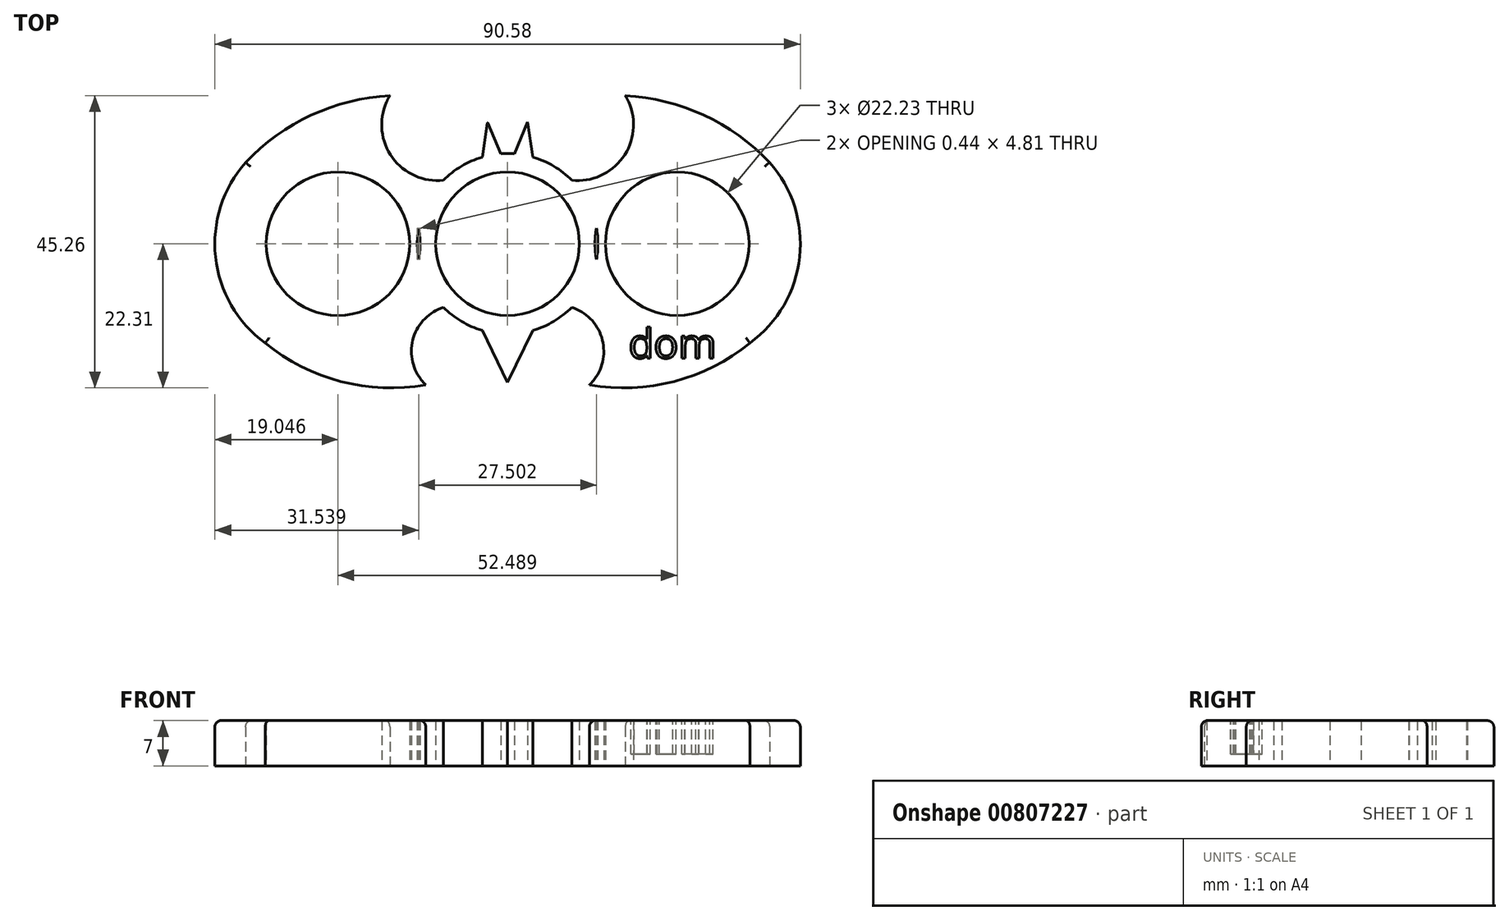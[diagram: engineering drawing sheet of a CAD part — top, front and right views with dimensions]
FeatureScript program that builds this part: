
annotation { "Feature Type Name" : "Feature", "Feature Type Description" : "" }
export const myFeature = defineFeature(function(context is Context, id is Id, definition is map)
    precondition{}
    {
        {
            var Q0;
            Q0=qCreatedBy(makeId("Top.planeOp"),FACE);
            var sketch = newSketch(context, id + "F0", { "sketchPlane" : qUnion([Q0])});
            skArc(sketch, "E0", {"start": v(-4.01, -13.38) * mm, "mid": v(7.2, 11.98) * mm, "end": v(-9.93, -9.83) * mm});
            skLineSegment(sketch, "E1", {"start": v(0, 0) * mm, "end": v(-26.24, 0) * mm});
            skLineSegment(sketch, "E2", {"start": v(0, 0) * mm, "end": v(26.24, 0) * mm});
            skArc(sketch, "E3", {"start": v(37.5, -15.37) * mm, "mid": v(45.18, -2.05) * mm, "end": v(40.53, 12.6) * mm});
            skArc(sketch, "E4", {"start": v(-18.2, 22.95) * mm, "mid": v(-30.36, 19.9) * mm, "end": v(-40.53, 12.6) * mm});
            skArc(sketch, "E5", {"start": v(-18.2, 22.95) * mm, "mid": v(-18.15, 13.81) * mm, "end": v(-9.93, 9.83) * mm});
            skArc(sketch, "E6.trimOffspring", {"start": v(-40.53, 12.6) * mm, "mid": v(-45.18, -2.05) * mm, "end": v(-37.5, -15.37) * mm});
            skArc(sketch, "E7.MirrorCS", {"start": v(18.2, 22.95) * mm, "mid": v(18.15, 13.81) * mm, "end": v(9.93, 9.83) * mm});
            skArc(sketch, "E8.MirrorCS", {"start": v(18.2, 22.95) * mm, "mid": v(30.36, 19.9) * mm, "end": v(40.53, 12.6) * mm});
            skArc(sketch, "E9", {"start": v(-37.5, -15.37) * mm, "mid": v(-25.79, -21.32) * mm, "end": v(-12.65, -21.85) * mm});
            skArc(sketch, "E10", {"start": v(-9.93, -9.83) * mm, "mid": v(-14.7, -15.06) * mm, "end": v(-12.65, -21.85) * mm});
            skArc(sketch, "E11.MirrorCS", {"start": v(9.93, -9.83) * mm, "mid": v(14.7, -15.06) * mm, "end": v(12.65, -21.85) * mm});
            skArc(sketch, "E12.MirrorCS", {"start": v(37.5, -15.37) * mm, "mid": v(25.79, -21.32) * mm, "end": v(12.65, -21.85) * mm});
            skPoint(sketch, "E13.end.orphan", {"position": v(2.34, 18.82) * mm});
            skPoint(sketch, "E14.orphan", {"position": v(3.92, 13.4) * mm});
            skPoint(sketch, "E15.end.orphan", {"position": v(-1.04, 13.93) * mm});
            skPoint(sketch, "E16.end.orphan", {"position": v(-2.23, 18.82) * mm});
            skPoint(sketch, "E17.MirrorCS.end.orphan", {"position": v(1.04, 13.93) * mm});
            skPoint(sketch, "E17.MirrorCS.start.orphan", {"position": v(2.23, 18.82) * mm});
            skPoint(sketch, "E18.end.orphan", {"position": v(-4.8, 18.35) * mm});
            skPoint(sketch, "E19.MirrorCS.end.orphan", {"position": v(4.8, 18.35) * mm});
            skLineSegment(sketch, "E20", {"start": v(-1.04, 13.93) * mm, "end": v(-3.1, 18.83) * mm});
            skLineSegment(sketch, "E21", {"start": v(-3.1, 18.83) * mm, "end": v(-3.92, 13.4) * mm});
            skLineSegment(sketch, "E22.MirrorCS", {"start": v(1.04, 13.93) * mm, "end": v(3.1, 18.83) * mm});
            skLineSegment(sketch, "E23.MirrorCS", {"start": v(3.1, 18.83) * mm, "end": v(3.92, 13.4) * mm});
            skPoint(sketch, "E24.end.orphan", {"position": v(0, -21.45) * mm});
            skPoint(sketch, "E24.start.orphan", {"position": v(-4.01, -13.38) * mm});
            skPoint(sketch, "E25.MirrorCS.start.orphan", {"position": v(4.01, -13.38) * mm});
            skPoint(sketch, "E26.MirrorCS.end.orphan", {"position": v(-3.92, -13.4) * mm});
            skPoint(sketch, "E26.MirrorCS.start.orphan", {"position": v(-3.1, -18.83) * mm});
            skLineSegment(sketch, "E27", {"start": v(-3.92, -13.4) * mm, "end": v(0, -21.45) * mm});
            skLineSegment(sketch, "E28.MirrorCS", {"start": v(3.92, -13.4) * mm, "end": v(0, -21.45) * mm});
            skLineSegment(sketch, "E29", {"start": v(0, 0) * mm, "end": v(45.3, 0) * mm});
            skArc(sketch, "E30", {"start": v(-13.76, -2.4) * mm, "mid": v(-13.53, 0) * mm, "end": v(-13.76, 2.4) * mm});
            skArc(sketch, "E31", {"start": v(13.76, 2.4) * mm, "mid": v(13.53, 0) * mm, "end": v(13.76, -2.4) * mm});
            skCircle(sketch, "E32", {"center": v(-26.24, 0) * mm, "radius": 11.11 * mm});
            skCircle(sketch, "E33", {"center": v(26.24, 0) * mm, "radius": 11.11 * mm});
            skCircle(sketch, "E34", {"center": v(0, 0) * mm, "radius": 13.97 * mm});
            skCircle(sketch, "E35", {"center": v(0, 0) * mm, "radius": 11.11 * mm});
            skSolve(sketch);
        }
        {
            var Q0;
            Q0=qSketchRegion(id+"F0",true);
            extrude(context, id + "F1", {"entities" : qUnion([Q0]), "depth" : 4.3 * mm, "offsetDistance" : 25.4 * mm});
        }
        {
            var Q0;
            Q0=qSketchRegion(id+"F0",true);
            extrude(context, id + "F2", {"entities" : qUnion([Q0]), "operationType" : NewBodyOperationType.ADD, "depth" : 7 * mm, "offsetDistance" : 25.4 * mm});
        }
        {
            var Q0;
            Q0=makeQuery(id+"F2.opExtrude","CAP_EDGE",EDGE,{"disambiguationData":[OSD([sQuery(id+"F0.wireOp",EDGE,"E6.trimOffspring")])],"isStart":false});
            var Q1;
            Q1=makeQuery(id+"F2.opExtrude","CAP_EDGE",EDGE,{"disambiguationData":[OSD([sQuery(id+"F0.wireOp",EDGE,"E4")])],"isStart":true});
            var Q2;
            Q2=makeQuery(id+"F2.opExtrude","CAP_EDGE",EDGE,{"disambiguationData":[OSD([sQuery(id+"F0.wireOp",EDGE,"E6.trimOffspring")])],"isStart":true});
            var Q3;
            Q3=makeQuery(id+"F2.opExtrude","CAP_EDGE",EDGE,{"disambiguationData":[OSD([sQuery(id+"F0.wireOp",EDGE,"E9")])],"isStart":true});
            fillet(context, id + "F3", {"entities" : qUnion([Q0, Q1, Q2, Q3]), "radius" : 1 * mm, "tangentPropagation" : true, "allowEdgeOverflow" : false});
        }
        {
            var Q0;
            Q0=makeQuery(id+"F2.opExtrude","CAP_EDGE",EDGE,{"disambiguationData":[OSD([sQuery(id+"F0.wireOp",EDGE,"E3")])],"isStart":false});
            var Q1;
            Q1=makeQuery(id+"F2.opExtrude","CAP_EDGE",EDGE,{"disambiguationData":[OSD([sQuery(id+"F0.wireOp",EDGE,"E3")])],"isStart":true});
            fillet(context, id + "F4", {"entities" : qUnion([Q0, Q1]), "radius" : 1 * mm, "tangentPropagation" : true, "allowEdgeOverflow" : false});
        }
        {
            var Q0;
            {var subQ0=sQuery(id+"F0.wireOp",EDGE,"E21");var subQ1=sQuery(id+"F0.wireOp",EDGE,"E20");Q0=makeQuery(id+"F2.boolean.opBoolean","MERGE",EDGE,{"derivedFrom":[makeQuery(id+"F1.opExtrude","SWEPT_EDGE",EDGE,{"disambiguationData":[OSD([subQ1,subQ0])]}),makeQuery(id+"F2.opExtrude","SWEPT_EDGE",EDGE,{"disambiguationData":[OSD([subQ1,subQ0])]})]});}
            fillet(context, id + "F5", {"entities" : qUnion([Q0]), "radius" : 0.04 * mm, "tangentPropagation" : true, "allowEdgeOverflow" : false});
        }
        {
            var Q0;
            Q0=makeQuery(id+"F2.opExtrude","CAP_FACE",FACE,{"disambiguationData":[OSD([sQuery(id+"F0.wireOp",EDGE,"E3"),sQuery(id+"F0.wireOp",EDGE,"E4"),sQuery(id+"F0.wireOp",EDGE,"E5"),sQuery(id+"F0.wireOp",EDGE,"E6.trimOffspring"),sQuery(id+"F0.wireOp",EDGE,"E7.MirrorCS"),sQuery(id+"F0.wireOp",EDGE,"E8.MirrorCS"),sQuery(id+"F0.wireOp",EDGE,"E9"),sQuery(id+"F0.wireOp",EDGE,"E10"),sQuery(id+"F0.wireOp",EDGE,"E11.MirrorCS"),sQuery(id+"F0.wireOp",EDGE,"E12.MirrorCS"),sQuery(id+"F0.wireOp",EDGE,"E20"),sQuery(id+"F0.wireOp",EDGE,"E21"),sQuery(id+"F0.wireOp",EDGE,"E22.MirrorCS"),sQuery(id+"F0.wireOp",EDGE,"E23.MirrorCS"),sQuery(id+"F0.wireOp",EDGE,"E27"),sQuery(id+"F0.wireOp",EDGE,"E28.MirrorCS"),sQuery(id+"F0.wireOp",EDGE,"E30"),sQuery(id+"F0.wireOp",EDGE,"E31"),sQuery(id+"F0.wireOp",EDGE,"E32"),sQuery(id+"F0.wireOp",EDGE,"E33"),sQuery(id+"F0.wireOp",EDGE,"E34"),sQuery(id+"F0.wireOp",EDGE,"E35")])],"isStart":false});
            var sketch = newSketch(context, id + "F6", { "sketchPlane" : qUnion([Q0])});
            skText(sketch, "E36", { "text": "dom\n\n", "fontName": "OpenSans-Regular.ttf"});
            const initialGuessF6  = {"E36": [0.01872, -0.01771, 1, 0, 0.00456]};
            skSetInitialGuess(sketch, initialGuessF6);
            skSolve(sketch);
        }
        {
            var Q0;
            Q0 = qSketchRegion(id + "F6", true);
            extrude(context, id + "F7", {"entities" : qUnion([Q0]), "operationType" : NewBodyOperationType.REMOVE, "oppositeDirection" : true, "depth" : 5.2 * mm, "offsetDistance" : 25 * mm});
        }
    });
